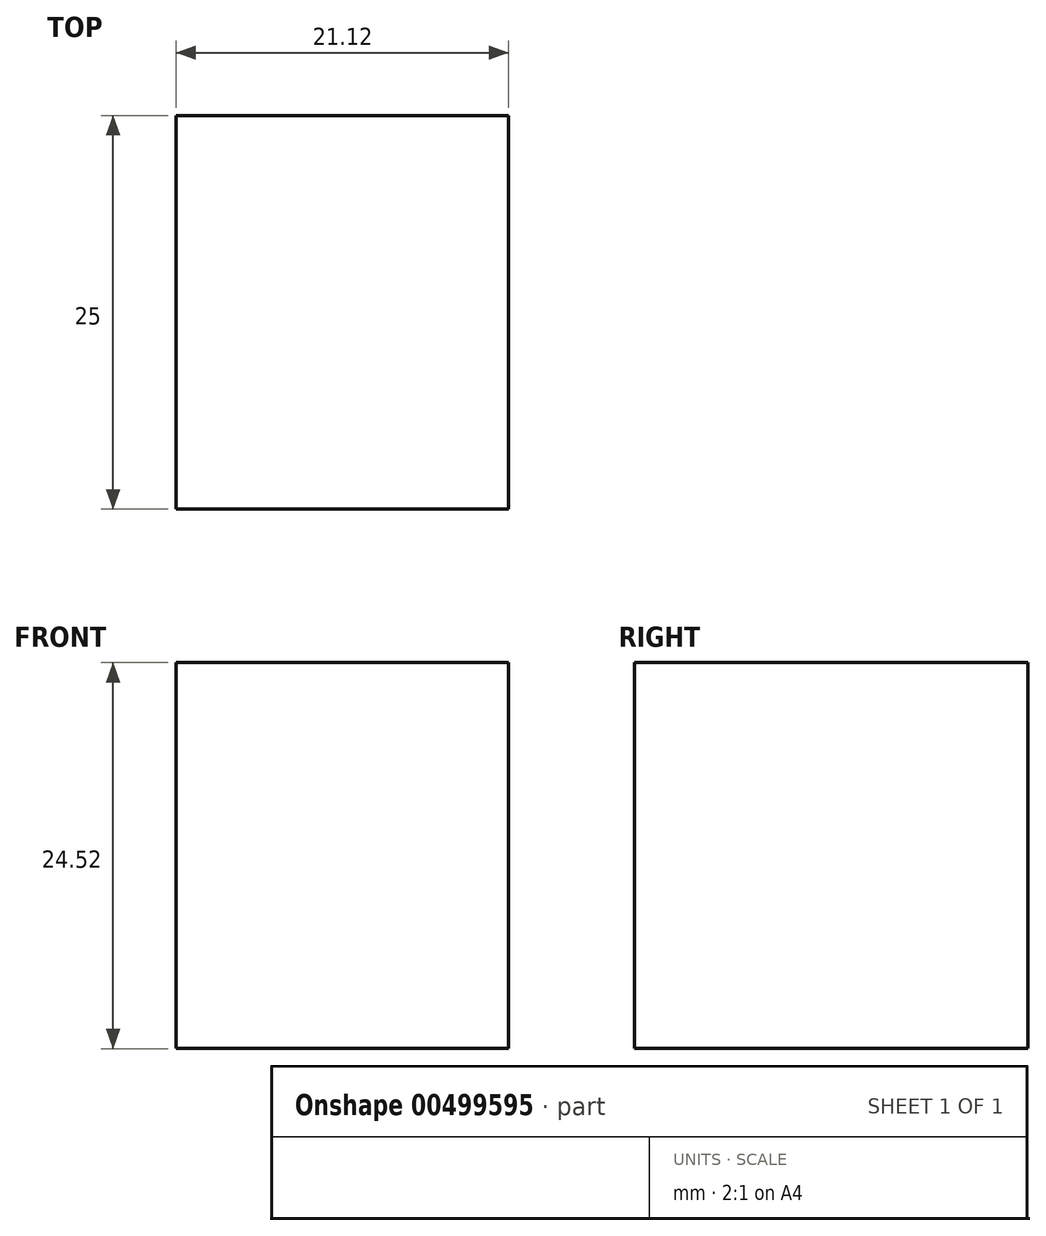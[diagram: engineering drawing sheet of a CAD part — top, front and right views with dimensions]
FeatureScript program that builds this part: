
annotation { "Feature Type Name" : "Feature", "Feature Type Description" : "" }
export const myFeature = defineFeature(function(context is Context, id is Id, definition is map)
    precondition{}
    {
        {
            var Q0;
            Q0=qCreatedBy(makeId("Front.planeOp"),FACE);
            var sketch = newSketch(context, id + "F0", { "sketchPlane" : qUnion([Q0])});
            skLineSegment(sketch, "E0.bottom", {"start": v(10.56, -12.26) * mm, "end": v(-10.56, -12.26) * mm});
            skLineSegment(sketch, "E0.top", {"start": v(10.56, 12.26) * mm, "end": v(-10.56, 12.26) * mm});
            skLineSegment(sketch, "E0.left", {"start": v(10.56, -12.26) * mm, "end": v(10.56, 12.26) * mm});
            skLineSegment(sketch, "E0.right", {"start": v(-10.56, -12.26) * mm, "end": v(-10.56, 12.26) * mm});
            skPoint(sketch, "E0.middle", {"position": v(0, 0) * mm});
            skSolve(sketch);
        }
        {
            var Q0;
            Q0 = qSketchRegion(id + "F0", true);
            extrude(context, id + "F1", {"entities" : qUnion([Q0]), "depth" : 25 * mm});
        }
    });
